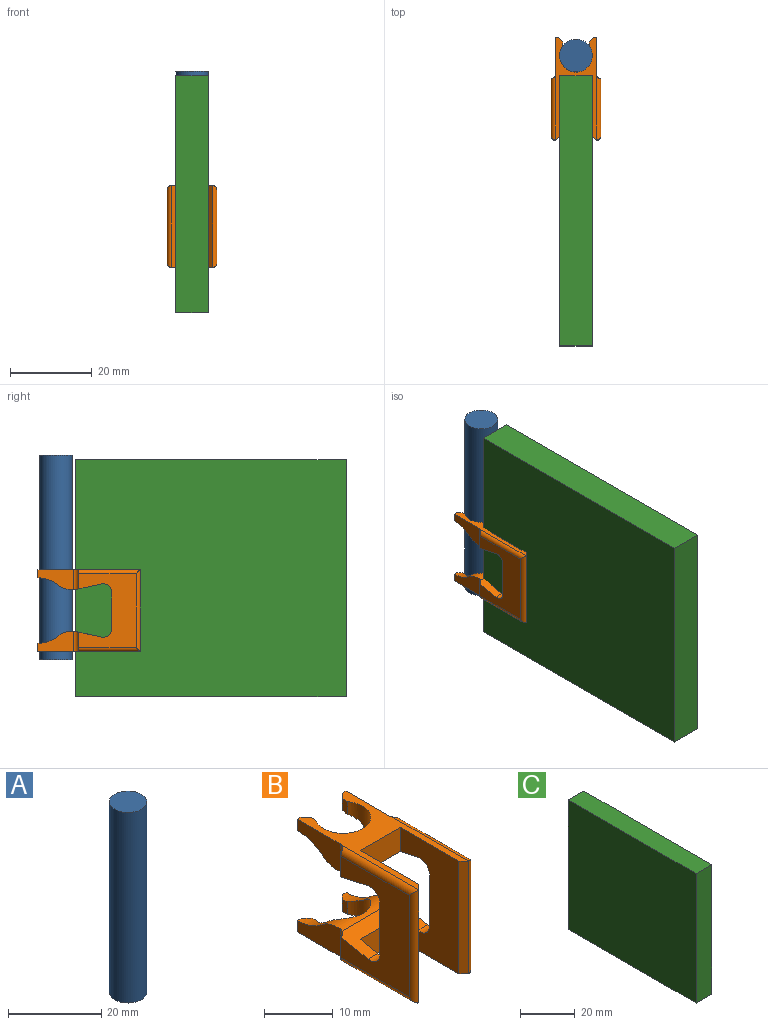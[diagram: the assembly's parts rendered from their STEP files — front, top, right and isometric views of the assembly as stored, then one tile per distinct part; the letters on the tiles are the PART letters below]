
ASSEMBLY  parts=3 mates=2
PART A: 3 faces, bbox 8x8x50 mm
  f0: cylinder r=4mm len=50mm, axis (0,0,-1), area 1256.6mm2, adj f1,f2
  f1: plane 8x8mm, normal (0,0,1), area 50.3mm2, adj f0
  f2: plane 8x8mm, normal (0,0,-1), area 50.3mm2, adj f0
PART B: 52 faces, bbox 12.3x25.1x20.1 mm
  f0: plane 2x0.75mm, normal (0,1,0), area 1.5mm2, adj f21,f23,f29,f51
  f1: plane 18x14mm, normal (-1,0,0), area 156.2mm2, adj f12,f13,f33,f34,f35,f38,f40,f42
  f2: plane 18x14mm, normal (1,0,0), area 156.2mm2, adj f10,f11,f30,f31,f32,f39,f41,f43
  f3: plane 20x12mm, normal (-1,0,0), area 166.3mm2, adj f5,f6,f20,f21,f37,f39,f41,f43
  f4: plane 20x12mm, normal (1,0,0), area 166.3mm2, adj f5,f6,f20,f21,f36,f38,f40,f42
  f5: plane 8.2x4.26mm, normal (0,-1,0), area 35mm2, adj f3,f4,f20,f44
  f6: plane 8.2x4.26mm, normal (0,-1,0), area 35mm2, adj f3,f4,f21,f45
  f7: plane 8.76x4.94mm, normal (-1,0,0), area 30.1mm2, adj f12,f20,f24,f46,f48
  f8: plane 8.76x4.94mm, normal (1,0,0), area 30.1mm2, adj f10,f19,f20,f46,f50
  f9: plane 2x0.75mm, normal (0,1,0), area 1.5mm2, adj f21,f22,f28,f49
  f10: cylinder r=1.25mm len=4.92mm, axis (0,0,1), area 8.5mm2, adj f2,f8,f20,f32,f44,f46
  f11: cylinder r=1.25mm len=4.92mm, axis (0,0,1), area 8.5mm2, adj f2,f21,f23,f30,f45,f47
  f12: cylinder r=1.25mm len=4.92mm, axis (0,0,1), area 8.5mm2, adj f1,f7,f20,f33,f44,f46
  f13: cylinder r=1.25mm len=4.92mm, axis (0,0,1), area 8.5mm2, adj f1,f21,f22,f35,f45,f47
  f14: plane 2.27x1.05mm, normal (-1,0,0), area 2.3mm2, adj f21,f27,f29,f51
  f15: plane 2.27x1.05mm, normal (1,0,0), area 2.3mm2, adj f21,f27,f28,f49
  f16: cylinder r=4mm len=8mm, axis (0,0,1), area 71.1mm2, adj f20,f25,f26,f46,f48,f50
  f17: plane 2.06x1mm, normal (0.71,0.71,0), area 2.9mm2, adj f20,f24,f26,f48
  f18: plane 2.06x1mm, normal (-0.71,0.71,0), area 2.9mm2, adj f19,f20,f25,f50
  f19: plane 2x0.75mm, normal (0,1,0), area 1.5mm2, adj f8,f18,f20,f50
  f20: plane 25x10.2mm, normal (0,0,-1), area 88.6mm2, adj f3,f4,f5,f7,f8,f10,f12,f16
  f21: plane 25x10.2mm, normal (0,0,1), area 88.6mm2, adj f0,f3,f4,f6,f9,f11,f13,f14
  f22: plane 8.76x4.94mm, normal (-1,0,0), area 30.1mm2, adj f9,f13,f21,f47,f49
  f23: plane 8.76x4.94mm, normal (1,0,0), area 30.1mm2, adj f0,f11,f21,f47,f51
  f24: plane 2x0.75mm, normal (0,1,0), area 1.5mm2, adj f7,f17,f20,f48
  f25: plane 2.27x1.05mm, normal (-1,0,0), area 2.3mm2, adj f16,f18,f20,f50
  f26: plane 2.27x1.05mm, normal (1,0,0), area 2.3mm2, adj f16,f17,f20,f48
  f27: cylinder r=4mm len=8mm, axis (0,0,1), area 71.1mm2, adj f14,f15,f21,f47,f49,f51
  f28: plane 2.06x1mm, normal (0.71,0.71,0), area 2.9mm2, adj f9,f15,f21,f49
  f29: plane 2.06x1mm, normal (-0.71,0.71,0), area 2.9mm2, adj f0,f14,f21,f51
  f30: cylinder r=1mm len=15.75mm, axis (0,1,0), area 23.2mm2, adj f2,f11,f21,f31
  f31: cylinder r=1mm len=20mm, axis (0,0,1), area 30.3mm2, adj f2,f30,f32,f37
  f32: cylinder r=1mm len=15.75mm, axis (0,1,0), area 23.2mm2, adj f2,f10,f20,f31
  f33: cylinder r=1mm len=15.75mm, axis (0,-1,0), area 23.2mm2, adj f1,f12,f20,f34
  f34: cylinder r=1mm len=20mm, axis (0,0,-1), area 30.3mm2, adj f1,f33,f35,f36
  f35: cylinder r=1mm len=15.75mm, axis (0,-1,0), area 23.2mm2, adj f1,f13,f21,f34
  f36: plane 20x1mm, normal (0.71,-0.71,0), area 28.3mm2, adj f4,f20,f21,f34
  f37: plane 20x1mm, normal (-0.71,-0.71,0), area 28.3mm2, adj f3,f20,f21,f31
  f38: cylinder r=2mm len=2.41mm, axis (1,0,0), area 7.1mm2, adj f1,f4,f40,f45
  f39: cylinder r=2mm len=2.41mm, axis (1,0,0), area 7.1mm2, adj f2,f3,f41,f45
  f40: plane 9.07x2mm, normal (0,1,0), area 18.1mm2, adj f1,f4,f38,f42
  f41: plane 9.07x2mm, normal (0,1,0), area 18.1mm2, adj f2,f3,f39,f43
  f42: cylinder r=2mm len=2.41mm, axis (1,0,0), area 7.1mm2, adj f1,f4,f40,f44
  f43: cylinder r=2mm len=2.41mm, axis (1,0,0), area 7.1mm2, adj f2,f3,f41,f44
  f44: plane 12.26x6.37mm, normal (0,-0.21,0.98), area 47.7mm2, adj f1,f2,f3,f4,f5,f10,f12,f42
  f45: plane 12.26x6.37mm, normal (0,-0.21,-0.98), area 47.7mm2, adj f1,f2,f3,f4,f6,f11,f13,f38
  f46: cylinder r=5mm len=10.22mm, axis (1,0,0), area 23.2mm2, adj f7,f8,f10,f12,f16,f44,f48,f50
  f47: cylinder r=5mm len=10.22mm, axis (1,0,0), area 23.2mm2, adj f11,f13,f22,f23,f27,f45,f49,f51
  f48: cylinder r=8mm len=5.07mm, axis (1,0,0), area 7.2mm2, adj f7,f16,f17,f24,f26,f46
  f49: cylinder r=8mm len=5.07mm, axis (1,0,0), area 7.2mm2, adj f9,f15,f22,f27,f28,f47
  f50: cylinder r=8mm len=5.07mm, axis (1,0,0), area 7.2mm2, adj f8,f16,f18,f19,f25,f46
  f51: cylinder r=8mm len=5.07mm, axis (1,0,0), area 7.2mm2, adj f0,f14,f23,f27,f29,f47
PART C: 6 faces, bbox 8x66.1x58 mm
  f0: plane 66.07x8mm, normal (0,0,-1), area 528.6mm2, adj f1,f3,f4,f5
  f1: plane 57.99x8mm, normal (0,1,0), area 463.9mm2, adj f0,f2,f4,f5
  f2: plane 66.07x8mm, normal (0,0,1), area 528.6mm2, adj f1,f3,f4,f5
  f3: plane 57.99x8mm, normal (0,-1,0), area 463.9mm2, adj f0,f2,f4,f5
  f4: plane 66.07x57.99mm, normal (1,0,0), area 3831.6mm2, adj f0,f1,f2,f3
  f5: plane 66.07x57.99mm, normal (-1,0,0), area 3831.6mm2, adj f0,f1,f2,f3
PLACE A t=(38.88,-66.91,4)mm
PLACE B t=(-10.71,-33.13,5.98)mm
PLACE C t=(-18.81,6.46,-5.14)mm fixed
MATE slider B.f16 <-> A.f0  axis (0,0,1) through (-14.81,-12.51,23.5)mm
MATE slider C.f1 <-> B.f6  axis (0,1,0) through (-14.81,-17.39,23.85)mm
